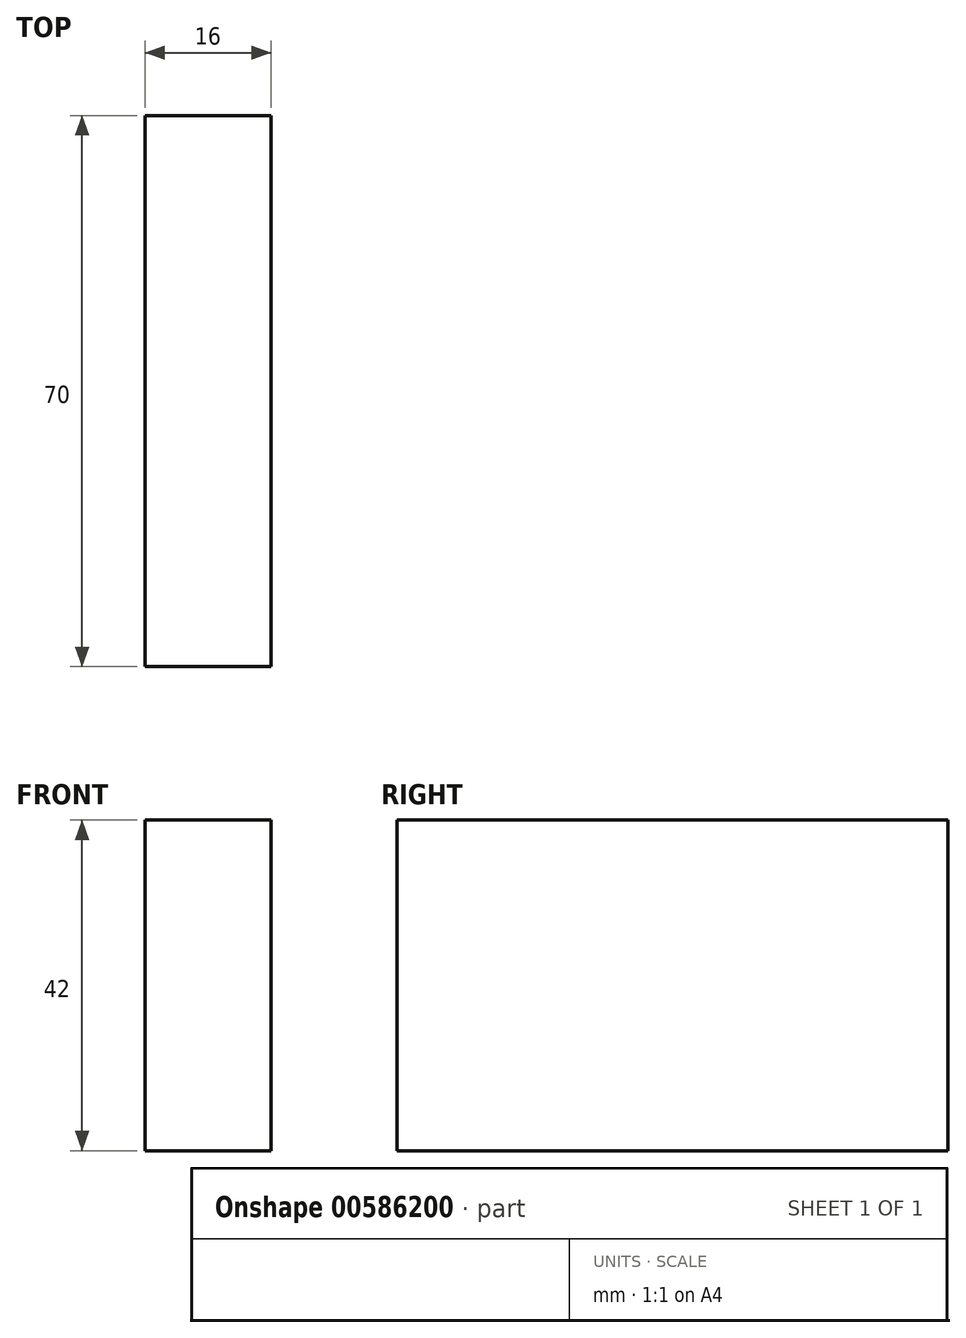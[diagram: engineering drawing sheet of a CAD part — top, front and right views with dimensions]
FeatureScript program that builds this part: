
annotation { "Feature Type Name" : "Feature", "Feature Type Description" : "" }
export const myFeature = defineFeature(function(context is Context, id is Id, definition is map)
    precondition{}
    {
        {
            var Q0;
            Q0=qCreatedBy(makeId("Top.planeOp"),FACE);
            var sketch = newSketch(context, id + "F0", { "sketchPlane" : qUnion([Q0])});
            skLineSegment(sketch, "E0.bottom", {"start": v(-8, 35) * mm, "end": v(8, 35) * mm});
            skLineSegment(sketch, "E0.top", {"start": v(-8, -35) * mm, "end": v(8, -35) * mm});
            skLineSegment(sketch, "E0.left", {"start": v(-8, 35) * mm, "end": v(-8, -35) * mm});
            skLineSegment(sketch, "E0.right", {"start": v(8, 35) * mm, "end": v(8, -35) * mm});
            skPoint(sketch, "E0.middle", {"position": v(0, 0) * mm});
            skSolve(sketch);
        }
        {
            var Q0;
            Q0=makeQuery(id+"F0.imprint","IMPRINT",FACE,{"disambiguationData":[TD([[makeQuery(id+"F0.imprint","IMPRINT",EDGE,{"derivedFrom":sQuery(id+"F0.wireOp",EDGE,"E0.bottom")}),-1.0]])]});
            extrude(context, id + "F1", {"entities" : qUnion([Q0]), "depth" : -42 * mm, "offsetDistance" : 25 * mm});
        }
    });
